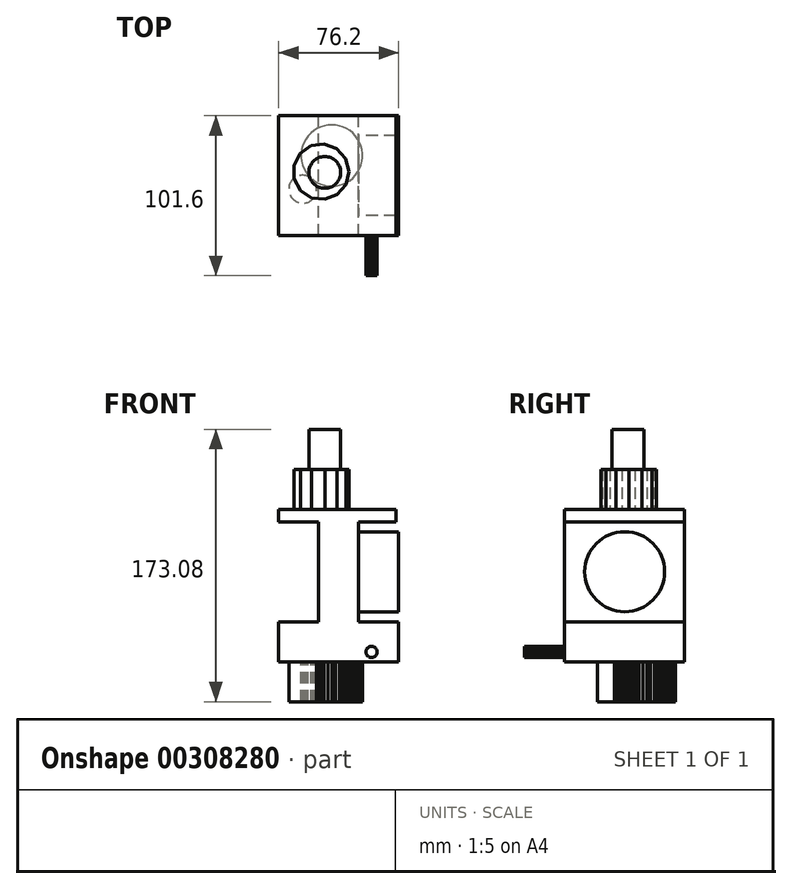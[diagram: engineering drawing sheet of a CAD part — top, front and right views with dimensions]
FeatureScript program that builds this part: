
annotation { "Feature Type Name" : "Feature", "Feature Type Description" : "" }
export const myFeature = defineFeature(function(context is Context, id is Id, definition is map)
    precondition{}
    {
        {
            var Q0;
            Q0=qCreatedBy(makeId("Front.planeOp"),FACE);
            var sketch = newSketch(context, id + "F0", { "sketchPlane" : qUnion([Q0])});
            skLineSegment(sketch, "E0", {"start": v(-43.63, -33.36) * mm, "end": v(32.57, -33.36) * mm});
            skLineSegment(sketch, "E1", {"start": v(32.57, -33.36) * mm, "end": v(32.57, -7.96) * mm});
            skLineSegment(sketch, "E2", {"start": v(7.17, -7.96) * mm, "end": v(32.57, -7.96) * mm});
            skLineSegment(sketch, "E3", {"start": v(7.17, -7.96) * mm, "end": v(7.17, 55.54) * mm});
            skLineSegment(sketch, "E4", {"start": v(7.17, 55.54) * mm, "end": v(30.76, 55.54) * mm});
            skLineSegment(sketch, "E5", {"start": v(30.76, 55.54) * mm, "end": v(30.76, 63.52) * mm});
            skLineSegment(sketch, "E6", {"start": v(30.76, 63.52) * mm, "end": v(-43.63, 63.52) * mm});
            skLineSegment(sketch, "E7", {"start": v(-43.63, 63.52) * mm, "end": v(-43.63, 55.54) * mm});
            skLineSegment(sketch, "E8", {"start": v(-43.63, 55.54) * mm, "end": v(-18.23, 55.54) * mm});
            skLineSegment(sketch, "E9", {"start": v(-18.23, 55.54) * mm, "end": v(-18.23, -7.96) * mm});
            skLineSegment(sketch, "E10", {"start": v(-18.23, -7.96) * mm, "end": v(-43.63, -7.96) * mm});
            skLineSegment(sketch, "E11", {"start": v(-43.63, -7.96) * mm, "end": v(-43.63, -33.36) * mm});
            skSolve(sketch);
        }
        {
            var Q0;
            Q0=makeQuery(id+"F0.imprint","IMPRINT",FACE,{"disambiguationData":[TD([[makeQuery(id+"F0.imprint","IMPRINT",EDGE,{"derivedFrom":sQuery(id+"F0.wireOp",EDGE,"E0")}),1.0]])]});
            extrude(context, id + "F1", {"entities" : qUnion([Q0]), "depth" : 76.2 * mm});
        }
        {
            var Q0;
            Q0=makeQuery(id+"F1.opExtrude","SWEPT_FACE",FACE,{"disambiguationData":[OSD([sQuery(id+"F0.wireOp",EDGE,"E3")])]});
            var sketch = newSketch(context, id + "F2", { "sketchPlane" : qUnion([Q0])});
            skCircle(sketch, "E12", {"center": v(-38.1, 23.8) * mm, "radius": 25.4 * mm});
            skPoint(sketch, "E12.centerSnap0", {"position": v(-76.2, 23.8) * mm});
            skPoint(sketch, "E12.centerSnap1", {"position": v(-38.1, 55.54) * mm});
            skSolve(sketch);
        }
        {
            var Q0;
            Q0=makeQuery(id+"F2.imprint","IMPRINT",FACE,{"disambiguationData":[TD([[makeQuery(id+"F2.imprint","IMPRINT",EDGE,{"derivedFrom":sQuery(id+"F2.wireOp",EDGE,"E12")}),1.0]])]});
            extrude(context, id + "F3", {"entities" : qUnion([Q0]), "operationType" : NewBodyOperationType.ADD, "depth" : 25.4 * mm});
        }
        {
            var Q0;
            Q0=makeQuery(id+"F1.opExtrude","SWEPT_FACE",FACE,{"disambiguationData":[OSD([sQuery(id+"F0.wireOp",EDGE,"E6")])]});
            var sketch = newSketch(context, id + "F4", { "sketchPlane" : qUnion([Q0])});
            skCircle(sketch, "E13.cCircle", {"center": v(-16.7, -35.52) * mm, "radius": 17.16 * mm, "construction": true});
            skLineSegment(sketch, "E13.0", {"start": v(0.97, -35.34) * mm, "end": v(-0.97, -43.58) * mm});
            skLineSegment(sketch, "E13.1", {"start": v(-0.97, -43.58) * mm, "end": v(-6.52, -49.96) * mm});
            skLineSegment(sketch, "E13.2", {"start": v(-6.52, -49.96) * mm, "end": v(-14.4, -53.04) * mm});
            skLineSegment(sketch, "E13.3", {"start": v(-14.4, -53.04) * mm, "end": v(-22.8, -52.1) * mm});
            skLineSegment(sketch, "E13.4", {"start": v(-22.8, -52.1) * mm, "end": v(-29.81, -47.37) * mm});
            skLineSegment(sketch, "E13.5", {"start": v(-29.81, -47.37) * mm, "end": v(-33.82, -39.92) * mm});
            skLineSegment(sketch, "E13.6", {"start": v(-33.82, -39.92) * mm, "end": v(-33.9, -31.46) * mm});
            skLineSegment(sketch, "E13.7", {"start": v(-33.9, -31.46) * mm, "end": v(-30.05, -23.93) * mm});
            skLineSegment(sketch, "E13.8", {"start": v(-30.05, -23.93) * mm, "end": v(-23.13, -19.06) * mm});
            skLineSegment(sketch, "E13.9", {"start": v(-23.13, -19.06) * mm, "end": v(-14.75, -17.96) * mm});
            skLineSegment(sketch, "E13.10", {"start": v(-14.75, -17.96) * mm, "end": v(-6.8, -20.88) * mm});
            skLineSegment(sketch, "E13.11", {"start": v(-6.8, -20.88) * mm, "end": v(-1.14, -27.15) * mm});
            skLineSegment(sketch, "E13.12", {"start": v(-1.14, -27.15) * mm, "end": v(0.97, -35.34) * mm});
            skPoint(sketch, "E13.0.midPoint", {"position": v(0, -39.46) * mm});
            skSolve(sketch);
        }
        {
            var Q0;
            Q0=makeQuery(id+"F4.imprint","IMPRINT",FACE,{"disambiguationData":[TD([[makeQuery(id+"F4.imprint","IMPRINT",EDGE,{"derivedFrom":sQuery(id+"F4.wireOp",EDGE,"E13.0")}),-1.0]])]});
            extrude(context, id + "F5", {"entities" : qUnion([Q0]), "operationType" : NewBodyOperationType.ADD, "depth" : 25.4 * mm});
        }
        {
            var Q0;
            Q0=makeQuery(id+"F5.opExtrude","CAP_FACE",FACE,{"disambiguationData":[OSD([sQuery(id+"F4.wireOp",EDGE,"E13.0"),sQuery(id+"F4.wireOp",EDGE,"E13.1"),sQuery(id+"F4.wireOp",EDGE,"E13.2"),sQuery(id+"F4.wireOp",EDGE,"E13.3"),sQuery(id+"F4.wireOp",EDGE,"E13.4"),sQuery(id+"F4.wireOp",EDGE,"E13.5"),sQuery(id+"F4.wireOp",EDGE,"E13.6"),sQuery(id+"F4.wireOp",EDGE,"E13.7"),sQuery(id+"F4.wireOp",EDGE,"E13.8"),sQuery(id+"F4.wireOp",EDGE,"E13.9"),sQuery(id+"F4.wireOp",EDGE,"E13.10"),sQuery(id+"F4.wireOp",EDGE,"E13.11"),sQuery(id+"F4.wireOp",EDGE,"E13.12")])],"isStart":false});
            var sketch = newSketch(context, id + "F6", { "sketchPlane" : qUnion([Q0])});
            skCircle(sketch, "E14", {"center": v(-14.4, -35.96) * mm, "radius": 10.09 * mm});
            skSolve(sketch);
        }
        {
            var Q0;
            Q0=makeQuery(id+"F6.imprint","IMPRINT",FACE,{"disambiguationData":[TD([[makeQuery(id+"F6.imprint","IMPRINT",EDGE,{"derivedFrom":sQuery(id+"F6.wireOp",EDGE,"E14")}),1.0]])]});
            extrude(context, id + "F7", {"entities" : qUnion([Q0]), "operationType" : NewBodyOperationType.ADD, "depth" : 25.4 * mm});
        }
        {
            var Q0;
            Q0=makeQuery(id+"F1.opExtrude","CAP_FACE",FACE,{"disambiguationData":[OSD([sQuery(id+"F0.wireOp",EDGE,"E0"),sQuery(id+"F0.wireOp",EDGE,"E1"),sQuery(id+"F0.wireOp",EDGE,"E2"),sQuery(id+"F0.wireOp",EDGE,"E3"),sQuery(id+"F0.wireOp",EDGE,"E4"),sQuery(id+"F0.wireOp",EDGE,"E5"),sQuery(id+"F0.wireOp",EDGE,"E6"),sQuery(id+"F0.wireOp",EDGE,"E7"),sQuery(id+"F0.wireOp",EDGE,"E8"),sQuery(id+"F0.wireOp",EDGE,"E9"),sQuery(id+"F0.wireOp",EDGE,"E10"),sQuery(id+"F0.wireOp",EDGE,"E11")])],"isStart":false});
            var sketch = newSketch(context, id + "F8", { "sketchPlane" : qUnion([Q0])});
            skCircle(sketch, "E15.cCircle", {"center": v(15.3, -27.14) * mm, "radius": 3.57 * mm, "construction": true});
            skLineSegment(sketch, "E15.0", {"start": v(11.73, -27.42) * mm, "end": v(11.73, -26.87) * mm});
            skLineSegment(sketch, "E15.1", {"start": v(11.73, -26.87) * mm, "end": v(11.81, -26.33) * mm});
            skLineSegment(sketch, "E15.2", {"start": v(11.81, -26.33) * mm, "end": v(11.98, -25.8) * mm});
            skLineSegment(sketch, "E15.3", {"start": v(11.98, -25.8) * mm, "end": v(12.22, -25.31) * mm});
            skLineSegment(sketch, "E15.4", {"start": v(12.22, -25.31) * mm, "end": v(12.54, -24.87) * mm});
            skLineSegment(sketch, "E15.5", {"start": v(12.54, -24.87) * mm, "end": v(12.92, -24.47) * mm});
            skLineSegment(sketch, "E15.6", {"start": v(12.92, -24.47) * mm, "end": v(13.35, -24.14) * mm});
            skLineSegment(sketch, "E15.7", {"start": v(13.35, -24.14) * mm, "end": v(13.83, -23.88) * mm});
            skLineSegment(sketch, "E15.8", {"start": v(13.83, -23.88) * mm, "end": v(14.35, -23.7) * mm});
            skLineSegment(sketch, "E15.9", {"start": v(14.35, -23.7) * mm, "end": v(14.89, -23.59) * mm});
            skLineSegment(sketch, "E15.10", {"start": v(14.89, -23.59) * mm, "end": v(15.43, -23.57) * mm});
            skLineSegment(sketch, "E15.11", {"start": v(15.43, -23.57) * mm, "end": v(15.98, -23.63) * mm});
            skLineSegment(sketch, "E15.12", {"start": v(15.98, -23.63) * mm, "end": v(16.5, -23.77) * mm});
            skLineSegment(sketch, "E15.13", {"start": v(16.5, -23.77) * mm, "end": v(17, -24) * mm});
            skLineSegment(sketch, "E15.14", {"start": v(17, -24) * mm, "end": v(17.46, -24.3) * mm});
            skLineSegment(sketch, "E15.15", {"start": v(17.46, -24.3) * mm, "end": v(17.87, -24.66) * mm});
            skLineSegment(sketch, "E15.16", {"start": v(17.87, -24.66) * mm, "end": v(18.22, -25.08) * mm});
            skLineSegment(sketch, "E15.17", {"start": v(18.22, -25.08) * mm, "end": v(18.5, -25.55) * mm});
            skLineSegment(sketch, "E15.18", {"start": v(18.5, -25.55) * mm, "end": v(18.7, -26.06) * mm});
            skLineSegment(sketch, "E15.19", {"start": v(18.7, -26.06) * mm, "end": v(18.83, -26.6) * mm});
            skLineSegment(sketch, "E15.20", {"start": v(18.83, -26.6) * mm, "end": v(18.87, -27.14) * mm});
            skLineSegment(sketch, "E15.21", {"start": v(18.87, -27.14) * mm, "end": v(18.83, -27.69) * mm});
            skLineSegment(sketch, "E15.22", {"start": v(18.83, -27.69) * mm, "end": v(18.7, -28.22) * mm});
            skLineSegment(sketch, "E15.23", {"start": v(18.7, -28.22) * mm, "end": v(18.5, -28.73) * mm});
            skLineSegment(sketch, "E15.24", {"start": v(18.5, -28.73) * mm, "end": v(18.22, -29.2) * mm});
            skLineSegment(sketch, "E15.25", {"start": v(18.22, -29.2) * mm, "end": v(17.87, -29.62) * mm});
            skLineSegment(sketch, "E15.26", {"start": v(17.87, -29.62) * mm, "end": v(17.46, -29.99) * mm});
            skLineSegment(sketch, "E15.27", {"start": v(17.46, -29.99) * mm, "end": v(17, -30.28) * mm});
            skLineSegment(sketch, "E15.28", {"start": v(17, -30.28) * mm, "end": v(16.5, -30.5) * mm});
            skLineSegment(sketch, "E15.29", {"start": v(16.5, -30.5) * mm, "end": v(15.98, -30.65) * mm});
            skLineSegment(sketch, "E15.30", {"start": v(15.98, -30.65) * mm, "end": v(15.43, -30.72) * mm});
            skLineSegment(sketch, "E15.31", {"start": v(15.43, -30.72) * mm, "end": v(14.89, -30.7) * mm});
            skLineSegment(sketch, "E15.32", {"start": v(14.89, -30.7) * mm, "end": v(14.35, -30.6) * mm});
            skLineSegment(sketch, "E15.33", {"start": v(14.35, -30.6) * mm, "end": v(13.83, -30.4) * mm});
            skLineSegment(sketch, "E15.34", {"start": v(13.83, -30.4) * mm, "end": v(13.35, -30.14) * mm});
            skLineSegment(sketch, "E15.35", {"start": v(13.35, -30.14) * mm, "end": v(12.92, -29.81) * mm});
            skLineSegment(sketch, "E15.36", {"start": v(12.92, -29.81) * mm, "end": v(12.54, -29.42) * mm});
            skLineSegment(sketch, "E15.37", {"start": v(12.54, -29.42) * mm, "end": v(12.22, -28.97) * mm});
            skLineSegment(sketch, "E15.38", {"start": v(12.22, -28.97) * mm, "end": v(11.98, -28.48) * mm});
            skLineSegment(sketch, "E15.39", {"start": v(11.98, -28.48) * mm, "end": v(11.81, -27.96) * mm});
            skLineSegment(sketch, "E15.40", {"start": v(11.81, -27.96) * mm, "end": v(11.73, -27.42) * mm});
            skPoint(sketch, "E15.0.midPoint", {"position": v(11.73, -27.14) * mm});
            skSolve(sketch);
        }
        {
            var Q0;
            Q0=makeQuery(id+"F8.imprint","IMPRINT",FACE,{"disambiguationData":[TD([[makeQuery(id+"F8.imprint","IMPRINT",EDGE,{"derivedFrom":sQuery(id+"F8.wireOp",EDGE,"E15.0")}),-1.0]])]});
            extrude(context, id + "F9", {"entities" : qUnion([Q0]), "operationType" : NewBodyOperationType.ADD, "depth" : 25.4 * mm});
        }
        {
            var Q0;
            Q0=makeQuery(id+"F1.opExtrude","SWEPT_FACE",FACE,{"disambiguationData":[OSD([sQuery(id+"F0.wireOp",EDGE,"E0")])]});
            var sketch = newSketch(context, id + "F10", { "sketchPlane" : qUnion([Q0])});
            skCircle(sketch, "E16", {"center": v(-28.39, 46.66) * mm, "radius": 8.87 * mm});
            skSolve(sketch);
        }
        {
            var Q0;
            Q0=makeQuery(id+"F10.imprint","IMPRINT",FACE,{"disambiguationData":[TD([[makeQuery(id+"F10.imprint","IMPRINT",EDGE,{"derivedFrom":sQuery(id+"F10.wireOp",EDGE,"E16")}),1.0]])]});
            extrude(context, id + "F11", {"entities" : qUnion([Q0]), "operationType" : NewBodyOperationType.ADD, "depth" : 25.4 * mm});
        }
        {
            var Q0;
            Q0=makeQuery(id+"F1.opExtrude","SWEPT_FACE",FACE,{"disambiguationData":[OSD([sQuery(id+"F0.wireOp",EDGE,"E0")])]});
            var sketch = newSketch(context, id + "F12", { "sketchPlane" : qUnion([Q0])});
            skCircle(sketch, "E17.cCircle", {"center": v(-9.94, 25.25) * mm, "radius": 19.42 * mm, "construction": true});
            skLineSegment(sketch, "E17.0", {"start": v(9.47, 26.47) * mm, "end": v(9.47, 24.03) * mm});
            skLineSegment(sketch, "E17.1", {"start": v(9.47, 24.03) * mm, "end": v(9.17, 21.6) * mm});
            skLineSegment(sketch, "E17.2", {"start": v(9.17, 21.6) * mm, "end": v(8.56, 19.24) * mm});
            skLineSegment(sketch, "E17.3", {"start": v(8.56, 19.24) * mm, "end": v(7.66, 16.97) * mm});
            skLineSegment(sketch, "E17.4", {"start": v(7.66, 16.97) * mm, "end": v(6.48, 14.83) * mm});
            skLineSegment(sketch, "E17.5", {"start": v(6.48, 14.83) * mm, "end": v(5.05, 12.85) * mm});
            skLineSegment(sketch, "E17.6", {"start": v(5.05, 12.85) * mm, "end": v(3.38, 11.07) * mm});
            skLineSegment(sketch, "E17.7", {"start": v(3.38, 11.07) * mm, "end": v(1.5, 9.51) * mm});
            skLineSegment(sketch, "E17.8", {"start": v(1.5, 9.51) * mm, "end": v(-0.57, 8.2) * mm});
            skLineSegment(sketch, "E17.9", {"start": v(-0.57, 8.2) * mm, "end": v(-2.78, 7.16) * mm});
            skLineSegment(sketch, "E17.10", {"start": v(-2.78, 7.16) * mm, "end": v(-5.1, 6.4) * mm});
            skLineSegment(sketch, "E17.11", {"start": v(-5.1, 6.4) * mm, "end": v(-7.5, 5.95) * mm});
            skLineSegment(sketch, "E17.12", {"start": v(-7.5, 5.95) * mm, "end": v(-9.94, 5.8) * mm});
            skLineSegment(sketch, "E17.13", {"start": v(-9.94, 5.8) * mm, "end": v(-12.38, 5.95) * mm});
            skLineSegment(sketch, "E17.14", {"start": v(-12.38, 5.95) * mm, "end": v(-14.78, 6.4) * mm});
            skLineSegment(sketch, "E17.15", {"start": v(-14.78, 6.4) * mm, "end": v(-17.1, 7.16) * mm});
            skLineSegment(sketch, "E17.16", {"start": v(-17.1, 7.16) * mm, "end": v(-19.31, 8.2) * mm});
            skLineSegment(sketch, "E17.17", {"start": v(-19.31, 8.2) * mm, "end": v(-21.38, 9.51) * mm});
            skLineSegment(sketch, "E17.18", {"start": v(-21.38, 9.51) * mm, "end": v(-23.26, 11.07) * mm});
            skLineSegment(sketch, "E17.19", {"start": v(-23.26, 11.07) * mm, "end": v(-24.93, 12.85) * mm});
            skLineSegment(sketch, "E17.20", {"start": v(-24.93, 12.85) * mm, "end": v(-26.37, 14.83) * mm});
            skLineSegment(sketch, "E17.21", {"start": v(-26.37, 14.83) * mm, "end": v(-27.54, 16.97) * mm});
            skLineSegment(sketch, "E17.22", {"start": v(-27.54, 16.97) * mm, "end": v(-28.44, 19.24) * mm});
            skLineSegment(sketch, "E17.23", {"start": v(-28.44, 19.24) * mm, "end": v(-29.05, 21.6) * mm});
            skLineSegment(sketch, "E17.24", {"start": v(-29.05, 21.6) * mm, "end": v(-29.36, 24.03) * mm});
            skLineSegment(sketch, "E17.25", {"start": v(-29.36, 24.03) * mm, "end": v(-29.36, 26.47) * mm});
            skLineSegment(sketch, "E17.26", {"start": v(-29.36, 26.47) * mm, "end": v(-29.05, 28.9) * mm});
            skLineSegment(sketch, "E17.27", {"start": v(-29.05, 28.9) * mm, "end": v(-28.44, 31.26) * mm});
            skLineSegment(sketch, "E17.28", {"start": v(-28.44, 31.26) * mm, "end": v(-27.54, 33.53) * mm});
            skLineSegment(sketch, "E17.29", {"start": v(-27.54, 33.53) * mm, "end": v(-26.37, 35.67) * mm});
            skLineSegment(sketch, "E17.30", {"start": v(-26.37, 35.67) * mm, "end": v(-24.93, 37.65) * mm});
            skLineSegment(sketch, "E17.31", {"start": v(-24.93, 37.65) * mm, "end": v(-23.26, 39.43) * mm});
            skLineSegment(sketch, "E17.32", {"start": v(-23.26, 39.43) * mm, "end": v(-21.38, 40.99) * mm});
            skLineSegment(sketch, "E17.33", {"start": v(-21.38, 40.99) * mm, "end": v(-19.31, 42.3) * mm});
            skLineSegment(sketch, "E17.34", {"start": v(-19.31, 42.3) * mm, "end": v(-17.1, 43.34) * mm});
            skLineSegment(sketch, "E17.35", {"start": v(-17.1, 43.34) * mm, "end": v(-14.78, 44.1) * mm});
            skLineSegment(sketch, "E17.36", {"start": v(-14.78, 44.1) * mm, "end": v(-12.38, 44.55) * mm});
            skLineSegment(sketch, "E17.37", {"start": v(-12.38, 44.55) * mm, "end": v(-9.94, 44.7) * mm});
            skLineSegment(sketch, "E17.38", {"start": v(-9.94, 44.7) * mm, "end": v(-7.5, 44.55) * mm});
            skLineSegment(sketch, "E17.39", {"start": v(-7.5, 44.55) * mm, "end": v(-5.1, 44.1) * mm});
            skLineSegment(sketch, "E17.40", {"start": v(-5.1, 44.1) * mm, "end": v(-2.78, 43.34) * mm});
            skLineSegment(sketch, "E17.41", {"start": v(-2.78, 43.34) * mm, "end": v(-0.57, 42.3) * mm});
            skLineSegment(sketch, "E17.42", {"start": v(-0.57, 42.3) * mm, "end": v(1.5, 40.99) * mm});
            skLineSegment(sketch, "E17.43", {"start": v(1.5, 40.99) * mm, "end": v(3.38, 39.43) * mm});
            skLineSegment(sketch, "E17.44", {"start": v(3.38, 39.43) * mm, "end": v(5.05, 37.65) * mm});
            skLineSegment(sketch, "E17.45", {"start": v(5.05, 37.65) * mm, "end": v(6.48, 35.67) * mm});
            skLineSegment(sketch, "E17.46", {"start": v(6.48, 35.67) * mm, "end": v(7.66, 33.53) * mm});
            skLineSegment(sketch, "E17.47", {"start": v(7.66, 33.53) * mm, "end": v(8.56, 31.26) * mm});
            skLineSegment(sketch, "E17.48", {"start": v(8.56, 31.26) * mm, "end": v(9.17, 28.9) * mm});
            skLineSegment(sketch, "E17.49", {"start": v(9.17, 28.9) * mm, "end": v(9.47, 26.47) * mm});
            skPoint(sketch, "E17.0.midPoint", {"position": v(9.47, 25.25) * mm});
            skSolve(sketch);
        }
        {
            var Q0;
            Q0=makeQuery(id+"F12.imprint","IMPRINT",FACE,{"disambiguationData":[TD([[makeQuery(id+"F12.imprint","IMPRINT",EDGE,{"derivedFrom":sQuery(id+"F12.wireOp",EDGE,"E17.0")}),-1.0]])]});
            extrude(context, id + "F13", {"entities" : qUnion([Q0]), "operationType" : NewBodyOperationType.ADD, "depth" : 25.4 * mm});
        }
    });
